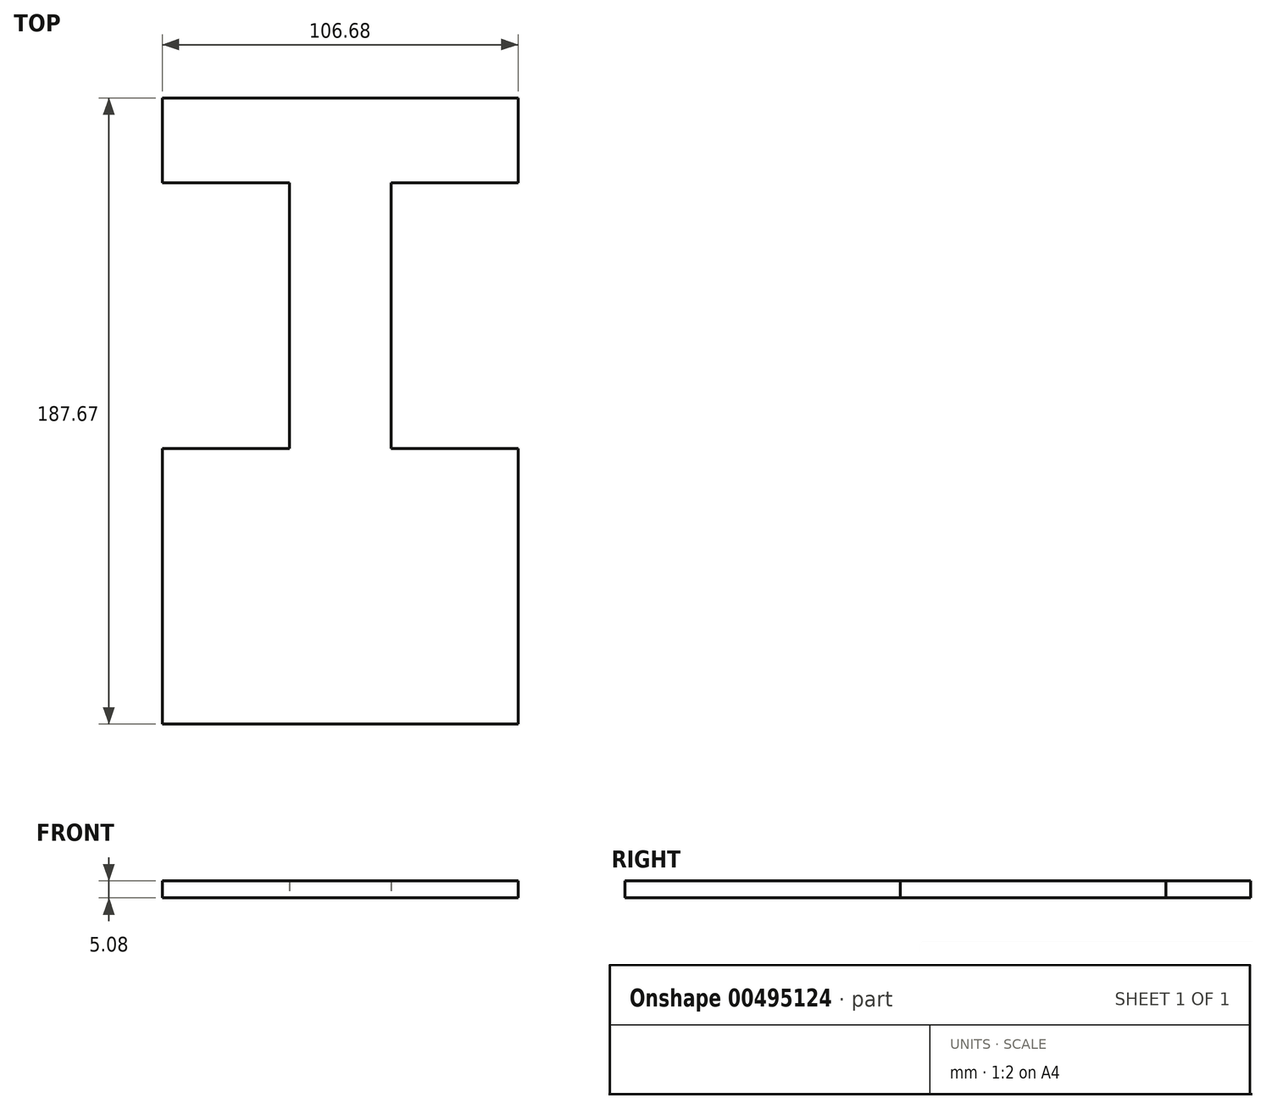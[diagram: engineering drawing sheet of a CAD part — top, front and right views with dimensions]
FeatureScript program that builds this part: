
annotation { "Feature Type Name" : "Feature", "Feature Type Description" : "" }
export const myFeature = defineFeature(function(context is Context, id is Id, definition is map)
    precondition{}
    {
        {
            var Q0;
            Q0=qCreatedBy(makeId("Top.planeOp"),FACE);
            var sketch = newSketch(context, id + "F0", { "sketchPlane" : qUnion([Q0])});
            skLineSegment(sketch, "E0", {"start": v(0, 169.34) * mm, "end": v(0, -123.9) * mm, "construction": true});
            skPoint(sketch, "E1", {"position": v(-20.2, 10.42) * mm});
            skPoint(sketch, "E2", {"position": v(20.2, 10.42) * mm});
            skLineSegment(sketch, "E3.0", {"start": v(-82.04, -62.24) * mm, "end": v(-82.04, -86.67) * mm});
            skFitSpline(sketch, "E3.1", {"points": [v(-89.63, 77.3) * mm, v(-84.78, 77.82) * mm, v(-75.8, 78.73) * mm, v(-64.34, 79.64) * mm, v(-54.63, 80.03) * mm, v(-46.36, 79.79) * mm, v(-40.42, 78.95) * mm, v(-36.08, 77.76) * mm, v(-33.03, 76.57) * mm, v(-30.2, 75.05) * mm, v(-27.63, 73.18) * mm, v(-25.36, 71) * mm, v(-23.43, 68.56) * mm, v(-21.82, 65.93) * mm, v(-20.48, 63.15) * mm, v(-19.35, 60.23) * mm, v(-18.54, 57.67) * mm, v(-17.95, 55.54) * mm, v(-17.38, 53.33) * mm, v(-16.72, 50.44) * mm, v(-16.02, 46.78) * mm, v(-15.17, 41.65) * mm, v(-14.32, 34.82) * mm, v(-13.62, 26.12) * mm, v(-13.28, 17.08) * mm, v(-13.33, 4.78) * mm, v(-14.19, -7.53) * mm, v(-16, -19.2) * mm, v(-17.87, -27.48) * mm, v(-19.93, -33.87) * mm, v(-21.93, -38.6) * mm, v(-23.62, -41.96) * mm, v(-25.54, -45.1) * mm, v(-27.67, -47.96) * mm, v(-30.03, -50.52) * mm, v(-32.58, -52.8) * mm, v(-35.3, -54.76) * mm, v(-39.14, -56.98) * mm, v(-44.24, -59.06) * mm, v(-50.7, -60.65) * mm, v(-57.5, -61.57) * mm, v(-64.65, -62.04) * mm, v(-74.74, -62.26) * mm, v(-82.99, -62.22) * mm, v(-88.83, -62.29) * mm]});
            skLineSegment(sketch, "E3.2", {"start": v(-82.04, -86.67) * mm, "end": v(0, -86.67) * mm});
            skLineSegment(sketch, "E3.3", {"start": v(-82.04, 101.72) * mm, "end": v(-82.04, 78.09) * mm});
            skLineSegment(sketch, "E3.4", {"start": v(0, 101.72) * mm, "end": v(-82.04, 101.72) * mm});
            skLineSegment(sketch, "E3.5", {"start": v(0, 101.72) * mm, "end": v(82.05, 101.72) * mm});
            skLineSegment(sketch, "E3.6", {"start": v(82.05, -86.67) * mm, "end": v(0, -86.67) * mm});
            skLineSegment(sketch, "E3.7", {"start": v(82.05, -62.24) * mm, "end": v(82.05, -86.67) * mm});
            skFitSpline(sketch, "E3.8", {"points": [v(89.64, 77.3) * mm, v(84.78, 77.82) * mm, v(75.81, 78.73) * mm, v(64.35, 79.64) * mm, v(54.63, 80.03) * mm, v(46.37, 79.79) * mm, v(40.42, 78.95) * mm, v(36.09, 77.76) * mm, v(33.04, 76.57) * mm, v(30.2, 75.05) * mm, v(27.63, 73.18) * mm, v(25.37, 71) * mm, v(23.44, 68.56) * mm, v(21.83, 65.93) * mm, v(20.49, 63.15) * mm, v(19.36, 60.23) * mm, v(18.55, 57.67) * mm, v(17.95, 55.54) * mm, v(17.39, 53.33) * mm, v(16.73, 50.44) * mm, v(16.02, 46.78) * mm, v(15.18, 41.65) * mm, v(14.32, 34.82) * mm, v(13.63, 26.12) * mm, v(13.29, 17.08) * mm, v(13.33, 4.78) * mm, v(14.2, -7.53) * mm, v(16, -19.2) * mm, v(17.88, -27.48) * mm, v(19.94, -33.87) * mm, v(21.93, -38.6) * mm, v(23.62, -41.96) * mm, v(25.54, -45.1) * mm, v(27.68, -47.96) * mm, v(30.03, -50.52) * mm, v(32.58, -52.8) * mm, v(35.31, -54.76) * mm, v(39.15, -56.98) * mm, v(44.24, -59.06) * mm, v(50.7, -60.65) * mm, v(57.5, -61.57) * mm, v(64.65, -62.04) * mm, v(74.74, -62.26) * mm, v(83, -62.22) * mm, v(88.83, -62.29) * mm]});
            skLineSegment(sketch, "E3.9", {"start": v(82.05, 101.72) * mm, "end": v(82.05, 78.09) * mm});
            skPoint(sketch, "E4.MirrorCS.start.orphan", {"position": v(0, 108.57) * mm});
            skPoint(sketch, "E5.start.orphan", {"position": v(88.9, 108.57) * mm});
            skPoint(sketch, "E6.MirrorCS.0.internal.orphan", {"position": v(-88.9, 70.47) * mm});
            skPoint(sketch, "E7.MirrorCS.start.orphan", {"position": v(-88.9, -55.43) * mm});
            skPoint(sketch, "E8.MirrorCS.end.orphan", {"position": v(0, -93.53) * mm});
            skPoint(sketch, "E8.MirrorCS.start.orphan", {"position": v(-88.9, -93.53) * mm});
            skPoint(sketch, "E9.0.internal.orphan", {"position": v(88.9, 70.47) * mm});
            skPoint(sketch, "E10.start.orphan", {"position": v(88.9, -55.43) * mm});
            skPoint(sketch, "E11.start.orphan", {"position": v(88.9, -93.53) * mm});
            skSolve(sketch);
        }
        {
            var Q0;
            Q0=qCreatedBy(makeId("Top.planeOp"),FACE);
            var sketch = newSketch(context, id + "F1", { "sketchPlane" : qUnion([Q0])});
            skLineSegment(sketch, "E12", {"start": v(0, 105.12) * mm, "end": v(53.34, 105.12) * mm});
            skLineSegment(sketch, "E13", {"start": v(53.34, 105.12) * mm, "end": v(53.34, 79.72) * mm});
            skLineSegment(sketch, "E14", {"start": v(53.34, 79.72) * mm, "end": v(15.24, 79.72) * mm});
            skLineSegment(sketch, "E15", {"start": v(15.24, 79.72) * mm, "end": v(15.24, 0) * mm});
            skLineSegment(sketch, "E16", {"start": v(15.24, 0) * mm, "end": v(53.34, 0) * mm});
            skLineSegment(sketch, "E17", {"start": v(53.34, 0) * mm, "end": v(53.34, -82.55) * mm});
            skLineSegment(sketch, "E18", {"start": v(53.34, -82.55) * mm, "end": v(0, -82.55) * mm});
            skLineSegment(sketch, "E19.MirrorCS", {"start": v(0, 105.12) * mm, "end": v(-53.34, 105.12) * mm});
            skLineSegment(sketch, "E20.MirrorCS", {"start": v(-53.34, -82.55) * mm, "end": v(0, -82.55) * mm});
            skLineSegment(sketch, "E21.MirrorCS", {"start": v(-15.24, 0) * mm, "end": v(-53.34, 0) * mm});
            skLineSegment(sketch, "E22.MirrorCS", {"start": v(-53.34, 79.72) * mm, "end": v(-15.24, 79.72) * mm});
            skLineSegment(sketch, "E23.MirrorCS", {"start": v(-15.24, 79.72) * mm, "end": v(-15.24, 0) * mm});
            skLineSegment(sketch, "E24.MirrorCS", {"start": v(-53.34, 0) * mm, "end": v(-53.34, -82.55) * mm});
            skLineSegment(sketch, "E25.MirrorCS", {"start": v(-53.34, 105.12) * mm, "end": v(-53.34, 79.72) * mm});
            skSolve(sketch);
        }
        {
            var Q0;
            Q0=makeQuery(id+"F1.imprint","IMPRINT",FACE,{"disambiguationData":[TD([[makeQuery(id+"F1.imprint","IMPRINT",EDGE,{"derivedFrom":sQuery(id+"F1.wireOp",EDGE,"E12")}),-1.0]])]});
            extrude(context, id + "F2", {"entities" : qUnion([Q0]), "depth" : 5.08 * mm, "offsetDistance" : 25.4 * mm});
        }
    });
